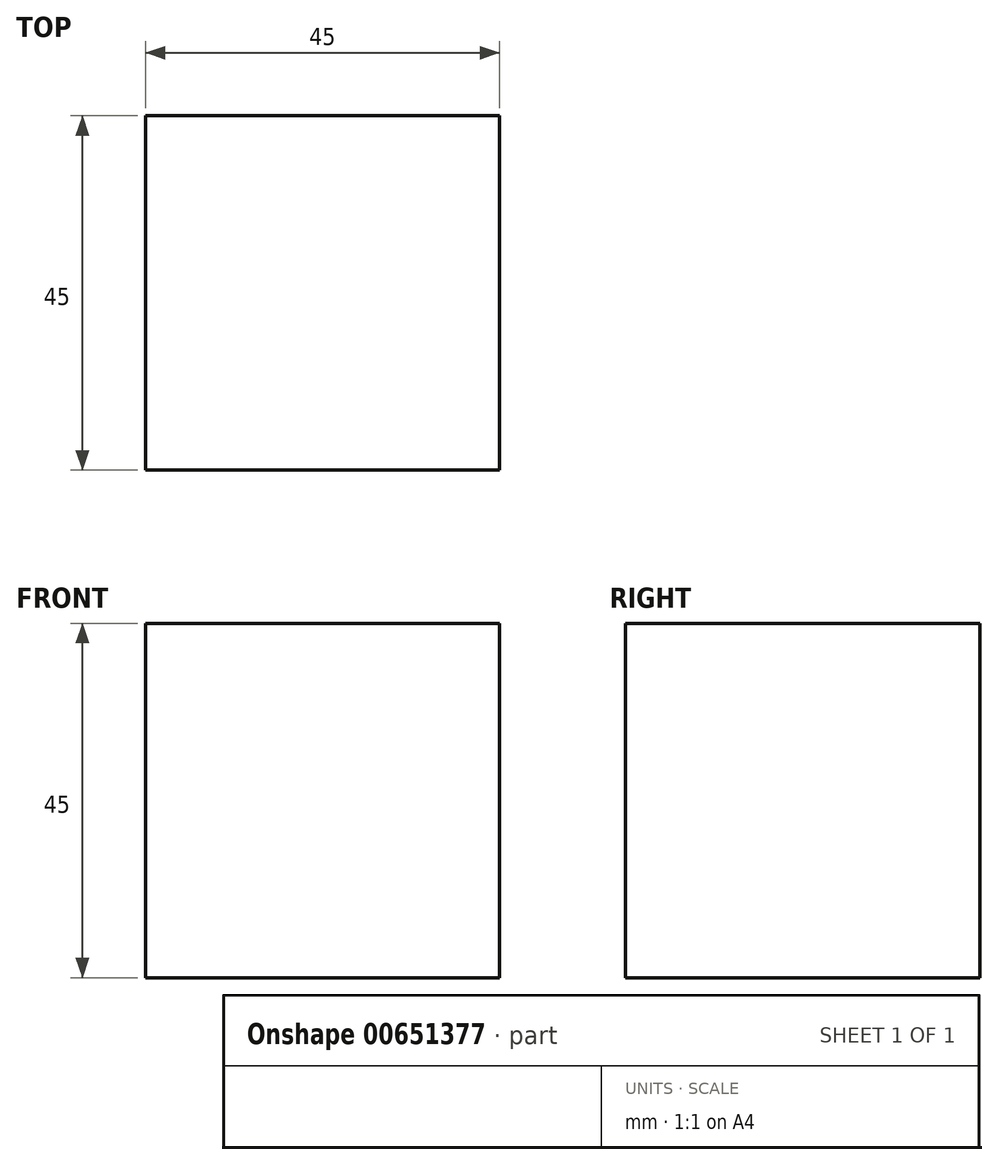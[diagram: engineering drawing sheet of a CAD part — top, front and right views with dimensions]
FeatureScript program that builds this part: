
annotation { "Feature Type Name" : "Feature", "Feature Type Description" : "" }
export const myFeature = defineFeature(function(context is Context, id is Id, definition is map)
    precondition{}
    {
        {
            var Q0;
            Q0=qCreatedBy(makeId("Right.planeOp"),FACE);
            var sketch = newSketch(context, id + "F0", { "sketchPlane" : qUnion([Q0])});
            skLineSegment(sketch, "E0.bottom", {"start": v(22.5, 22.5) * mm, "end": v(-22.5, 22.5) * mm});
            skLineSegment(sketch, "E0.top", {"start": v(22.5, -22.5) * mm, "end": v(-22.5, -22.5) * mm});
            skLineSegment(sketch, "E0.left", {"start": v(22.5, 22.5) * mm, "end": v(22.5, -22.5) * mm});
            skLineSegment(sketch, "E0.right", {"start": v(-22.5, 22.5) * mm, "end": v(-22.5, -22.5) * mm});
            skPoint(sketch, "E0.middle", {"position": v(0, 0) * mm});
            skSolve(sketch);
        }
        {
            var Q0;
            Q0 = qSketchRegion(id + "F0", true);
            extrude(context, id + "F1", {"entities" : qUnion([Q0]), "depth" : 45 * mm, "offsetDistance" : 25 * mm});
        }
    });
